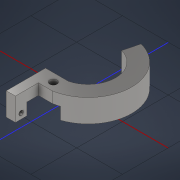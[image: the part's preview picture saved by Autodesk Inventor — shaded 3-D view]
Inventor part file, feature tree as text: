
AUTODESK INVENTOR PART (.ipt)
format: ipt  version: 2021 (Build 250183000, 183)  size: 178,688 bytes
history: native  units: mm
features: sketch x6, extrude x5, other x3, hole x2, projected_geometry x1
ambient origin geometry x8: Origin, YZ Plane, XZ Plane, XY Plane, X Axis, Y Axis, Z Axis, Center Point
bodies: Solid1 (feature_tree)
feature tree (17):
  extrude  "clamp"  Depth=12.0mm
  other  "reduction"
  other  "reductionSplit"
  extrude  "arm_c"  Depth=5.0mm
  extrude  "arb_b"  Depth=10.0mm TaperAngle=0.0deg
  hole  "pinHole"  [1 undecoded]
  extrude  "halfcut"  Depth=10.0mm TaperAngle=0.0deg
  extrude  "Extrusion6"  Depth=10.0mm TaperAngle=0.0deg
  hole  "cableHole"  [1 undecoded]
  other  "clawBase"
  sketch  "Sketch7"  dims[d3=12.0mm d5=7.0mm]
  projected_geometry  "Projected Loop2"
  sketch  "Sketch8"  dims[d6=0.0mm d7=5.0mm]
  sketch  "Sketch9"  dims[d8=3.0mm d9=10.0mm d10=0.0mm]
  sketch  "Sketch10"  dims[d11=12.0mm d12=0.0mm]
  sketch  "Sketch11"  dims[d14=-3.0mm d33=10.0mm d34=0.0mm]
  sketch  "Sketch12"  dims[d35=4.0mm d36=10.0mm d37=0.0mm d39=7.142713mm d41=0.0mm d42=3.571357mm d43=3.25mm d44=6.0mm d45=4.0mm d46=2.0mm d47=90.0deg d48=8.0mm d49=0.0mm d50=5.25mm d51=4.25mm d52=0.0mm d56=2.137935mm d57=2.0mm d58=6.0mm d59=4.0mm d60=2.0mm d61=90.0deg d62=8.0mm d63=0.0mm d64=3.0mm d65=0.0mm d66=19.75mm d67=0.0mm d68=5.0mm d69=10.0mm d70=0.0mm d71=2.5mm d72=2.375mm d15=0.872665mm d16=0.5mm d17=0.872665mm d73=0.5mm d74=0.872665mm]
note: 2 required parameter values undecoded (feature->parameter linkage not recoverable at this tier; creation-order binding heuristic only, values carry confidence <= 0.55)
